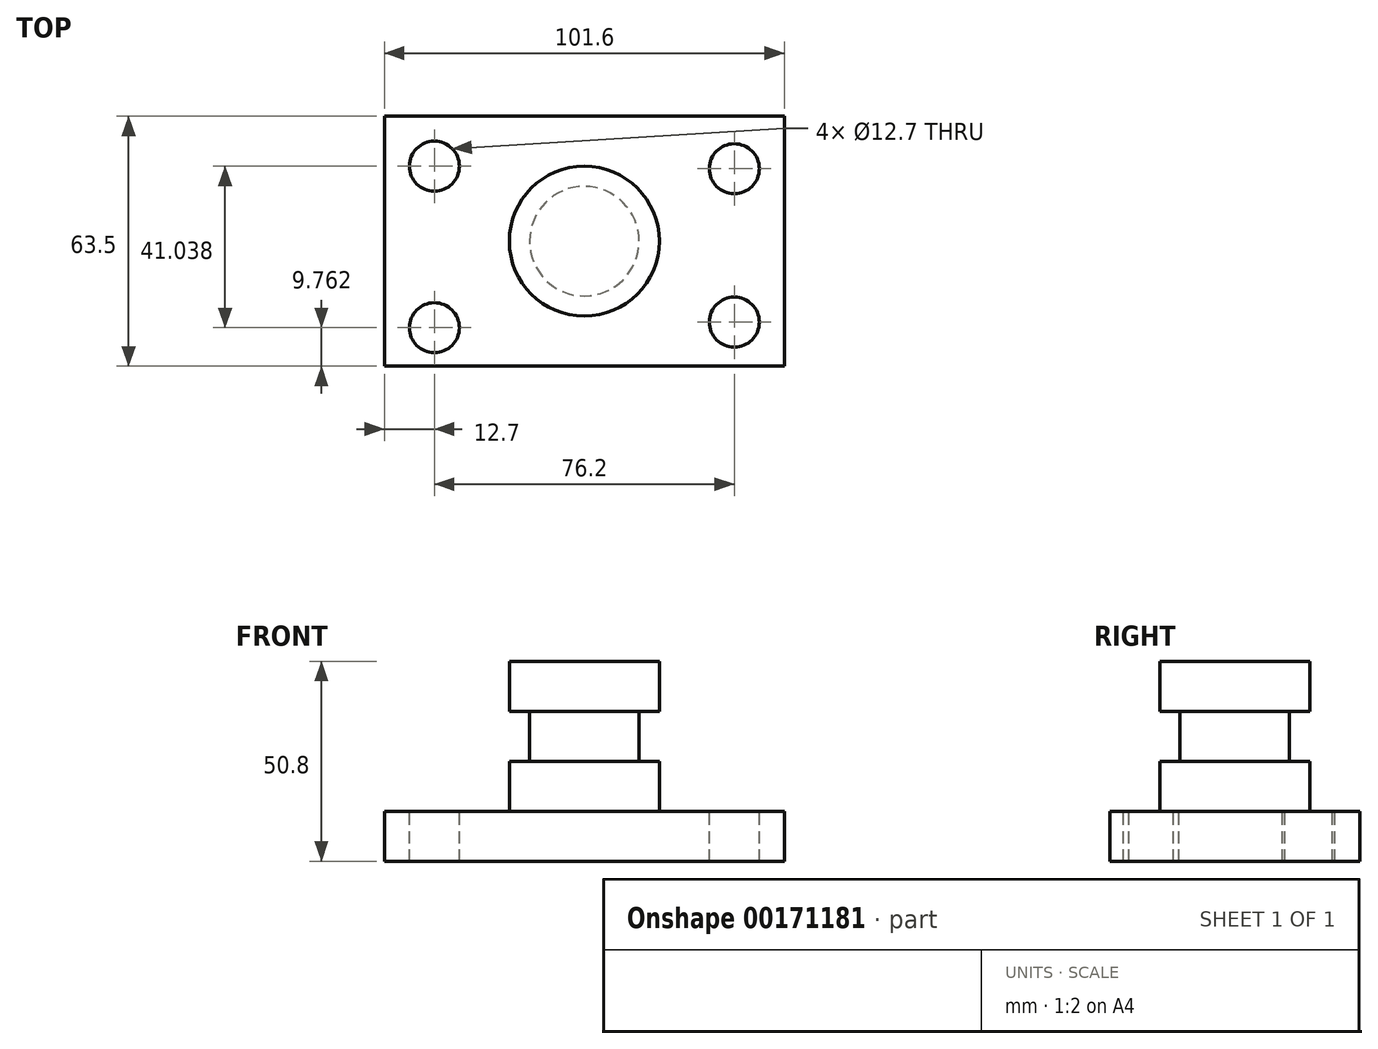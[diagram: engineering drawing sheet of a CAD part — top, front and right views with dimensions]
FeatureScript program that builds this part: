
annotation { "Feature Type Name" : "Feature", "Feature Type Description" : "" }
export const myFeature = defineFeature(function(context is Context, id is Id, definition is map)
    precondition{}
    {
        {
            var Q0;
            Q0=qCreatedBy(makeId("Top.planeOp"),FACE);
            var sketch = newSketch(context, id + "F0", { "sketchPlane" : qUnion([Q0])});
            skLineSegment(sketch, "E0.bottom", {"start": v(-36.65, 0) * mm, "end": v(36.65, 0) * mm});
            skLineSegment(sketch, "E0.left", {"start": v(-36.65, 0) * mm, "end": v(-36.65, 0) * mm});
            skLineSegment(sketch, "E0.right", {"start": v(36.65, 0) * mm, "end": v(36.65, 0) * mm});
            skPoint(sketch, "E0.middle", {"position": v(0, 0) * mm});
            skLineSegment(sketch, "E1.bottom", {"start": v(-50.8, 31.75) * mm, "end": v(50.8, 31.75) * mm});
            skLineSegment(sketch, "E1.top", {"start": v(-50.8, -31.75) * mm, "end": v(50.8, -31.75) * mm});
            skLineSegment(sketch, "E1.left", {"start": v(-50.8, 31.75) * mm, "end": v(-50.8, -31.75) * mm});
            skLineSegment(sketch, "E1.right", {"start": v(50.8, 31.75) * mm, "end": v(50.8, -31.75) * mm});
            skSolve(sketch);
        }
        {
            var Q0;
            Q0=makeQuery(id+"F0.imprint","IMPRINT",FACE,{"disambiguationData":[TD([[makeQuery(id+"F0.imprint","IMPRINT",EDGE,{"derivedFrom":sQuery(id+"F0.wireOp",EDGE,"E1.bottom")}),-1.0]])]});
            extrude(context, id + "F1", {"entities" : qUnion([Q0]), "depth" : 12.7 * mm});
        }
        {
            var Q0;
            Q0=makeQuery(id+"F1.opExtrude","CAP_FACE",FACE,{"disambiguationData":[OSD([sQuery(id+"F0.wireOp",EDGE,"E1.bottom"),sQuery(id+"F0.wireOp",EDGE,"E1.top"),sQuery(id+"F0.wireOp",EDGE,"E1.left"),sQuery(id+"F0.wireOp",EDGE,"E1.right")])],"isStart":false});
            var sketch = newSketch(context, id + "F2", { "sketchPlane" : qUnion([Q0])});
            skCircle(sketch, "E2", {"center": v(-38.1, 19.05) * mm, "radius": 6.35 * mm});
            skCircle(sketch, "E3", {"center": v(-38.1, -21.99) * mm, "radius": 6.35 * mm});
            skCircle(sketch, "E4", {"center": v(38.1, 18.41) * mm, "radius": 6.35 * mm});
            skCircle(sketch, "E5", {"center": v(38.1, -20.57) * mm, "radius": 6.35 * mm});
            skSolve(sketch);
        }
        {
            var Q0;
            Q0 = qSketchRegion(id + "F2", true);
            extrude(context, id + "F3", {"entities" : qUnion([Q0]), "operationType" : NewBodyOperationType.REMOVE, "endBound" : BoundingType.THROUGH_ALL, "oppositeDirection" : true, "depth" : 25.4 * mm});
        }
        {
            var Q0;
            Q0=qCreatedBy(makeId("Front.planeOp"),FACE);
            var sketch = newSketch(context, id + "F4", { "sketchPlane" : qUnion([Q0])});
            skLineSegment(sketch, "E6.bottom", {"start": v(0, 50.8) * mm, "end": v(-19.05, 50.8) * mm});
            skLineSegment(sketch, "E6.top", {"start": v(0, 12.7) * mm, "end": v(-19.05, 12.7) * mm});
            skLineSegment(sketch, "E6.left", {"start": v(0, 50.8) * mm, "end": v(0, 12.7) * mm});
            skLineSegment(sketch, "E6.right", {"start": v(-19.05, 50.8) * mm, "end": v(-19.05, 12.7) * mm});
            skSolve(sketch);
        }
        {
            var Q0;
            Q0=makeQuery(id+"F4.imprint","IMPRINT",FACE,{"disambiguationData":[TD([[makeQuery(id+"F4.imprint","IMPRINT",EDGE,{"derivedFrom":sQuery(id+"F4.wireOp",EDGE,"E6.bottom")}),1.0]])]});
            var Q1;
            Q1=sQuery(id+"F4.wireOp",EDGE,"E6.left");
            revolve(context, id + "F5", {"operationType" : NewBodyOperationType.ADD, "entities" : qUnion([Q0]), "axis" : qUnion([Q1]), "revolveType" : RevolveType.FULL});
        }
        {
            var Q0;
            Q0=qCreatedBy(makeId("Front.planeOp"),FACE);
            var sketch = newSketch(context, id + "F6", { "sketchPlane" : qUnion([Q0])});
            skLineSegment(sketch, "E7.bottom", {"start": v(-25.54, 25.4) * mm, "end": v(-13.91, 25.4) * mm});
            skLineSegment(sketch, "E7.top", {"start": v(-25.54, 38.1) * mm, "end": v(-13.91, 38.1) * mm});
            skLineSegment(sketch, "E7.left", {"start": v(-25.54, 25.4) * mm, "end": v(-25.54, 38.1) * mm});
            skLineSegment(sketch, "E7.right", {"start": v(-13.91, 25.4) * mm, "end": v(-13.91, 38.1) * mm});
            skPoint(sketch, "E7.middle", {"position": v(-19.73, 31.75) * mm});
            skLineSegment(sketch, "E8", {"start": v(0, 0) * mm, "end": v(0, 57.3) * mm});
            skSolve(sketch);
        }
        {
            var Q0;
            Q0=makeQuery(id+"F6.imprint","IMPRINT",FACE,{"disambiguationData":[TD([[makeQuery(id+"F6.imprint","IMPRINT",EDGE,{"derivedFrom":sQuery(id+"F6.wireOp",EDGE,"E7.bottom")}),1.0]])]});
            var Q1;
            Q1=sQuery(id+"F6.wireOp",EDGE,"E8");
            revolve(context, id + "F7", {"operationType" : NewBodyOperationType.REMOVE, "entities" : qUnion([Q0]), "axis" : qUnion([Q1]), "revolveType" : RevolveType.FULL, "oppositeDirection" : true});
        }
    });
